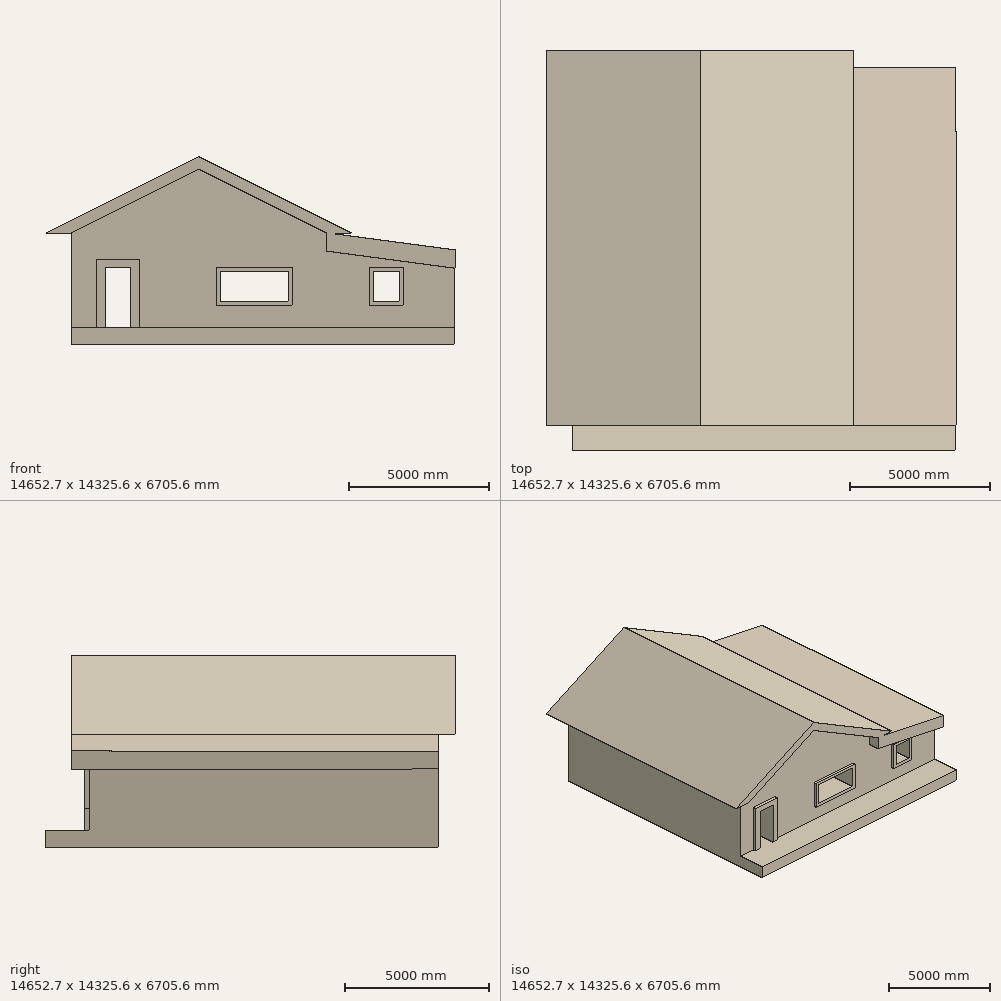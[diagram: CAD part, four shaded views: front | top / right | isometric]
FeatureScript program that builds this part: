
annotation { "Feature Type Name" : "Feature", "Feature Type Description" : "" }
export const myFeature = defineFeature(function(context is Context, id is Id, definition is map)
    precondition{}
    {
        {
            var Q0;
            Q0=qCreatedBy(makeId("Front.planeOp"),FACE);
            var sketch = newSketch(context, id + "F0", { "sketchPlane" : qUnion([Q0])});
            skLineSegment(sketch, "E0", {"start": v(0, 0) * mm, "end": v(4572, 0) * mm});
            skLineSegment(sketch, "E1", {"start": v(0, 0) * mm, "end": v(-4572, 0) * mm});
            skLineSegment(sketch, "E2", {"start": v(0, 0) * mm, "end": v(0, 2286) * mm});
            skLineSegment(sketch, "E3", {"start": v(0, 2286) * mm, "end": v(0, 2743.2) * mm});
            skLineSegment(sketch, "E4", {"start": v(-4572, 0) * mm, "end": v(-5486.4, 0) * mm});
            skLineSegment(sketch, "E5", {"start": v(4572, 0) * mm, "end": v(5486.4, 0) * mm});
            skLineSegment(sketch, "E6", {"start": v(0, 2286) * mm, "end": v(4572, 0) * mm});
            skLineSegment(sketch, "E7", {"start": v(0, 2286) * mm, "end": v(-4572, 0) * mm});
            skLineSegment(sketch, "E8", {"start": v(0, 2743.2) * mm, "end": v(-5486.4, 0) * mm});
            skLineSegment(sketch, "E9", {"start": v(0, 2743.2) * mm, "end": v(5486.4, 0) * mm});
            skLineSegment(sketch, "E10", {"start": v(-4572, 0) * mm, "end": v(-4572, -3352.8) * mm});
            skLineSegment(sketch, "E11", {"start": v(-4572, -3352.8) * mm, "end": v(4572, -3352.8) * mm});
            skLineSegment(sketch, "E12", {"start": v(4572, 0) * mm, "end": v(4572, -609.6) * mm});
            skLineSegment(sketch, "E13", {"start": v(4572, -609.6) * mm, "end": v(4572, -3352.8) * mm});
            skLineSegment(sketch, "E14", {"start": v(-4572, -3352.8) * mm, "end": v(-4572, -3962.4) * mm});
            skLineSegment(sketch, "E15", {"start": v(-4572, -3962.4) * mm, "end": v(4572, -3962.4) * mm});
            skLineSegment(sketch, "E16", {"start": v(4572, -3352.8) * mm, "end": v(4572, -3962.4) * mm});
            skLineSegment(sketch, "E17", {"start": v(4572, -3962.4) * mm, "end": v(9144, -3962.4) * mm});
            skLineSegment(sketch, "E18", {"start": v(4572, -3352.8) * mm, "end": v(9144, -3352.8) * mm});
            skLineSegment(sketch, "E19", {"start": v(9144, -3352.8) * mm, "end": v(9144, -3962.4) * mm});
            skLineSegment(sketch, "E20", {"start": v(9144, -3352.8) * mm, "end": v(9144, -609.6) * mm});
            skLineSegment(sketch, "E21", {"start": v(4572, 0) * mm, "end": v(9144, -609.6) * mm});
            skLineSegment(sketch, "E22", {"start": v(9144, -609.6) * mm, "end": v(9144, -1219.2) * mm});
            skLineSegment(sketch, "E23", {"start": v(4572, -609.6) * mm, "end": v(9144, -1219.2) * mm});
            skLineSegment(sketch, "E24", {"start": v(-3352.8, -3352.8) * mm, "end": v(-3352.8, -1219.2) * mm});
            skLineSegment(sketch, "E25", {"start": v(-2438.4, -3352.8) * mm, "end": v(-2438.4, -1219.2) * mm});
            skLineSegment(sketch, "E26", {"start": v(-2438.4, -1219.2) * mm, "end": v(-3352.8, -1219.2) * mm});
            skLineSegment(sketch, "E27", {"start": v(-3657.6, -3352.8) * mm, "end": v(-3657.6, -914.4) * mm});
            skLineSegment(sketch, "E28", {"start": v(-3657.6, -914.4) * mm, "end": v(-2133.6, -914.4) * mm});
            skLineSegment(sketch, "E29", {"start": v(-2133.6, -914.4) * mm, "end": v(-2133.6, -3352.8) * mm});
            skLineSegment(sketch, "E30.bottom", {"start": v(609.6, -1219.2) * mm, "end": v(3352.8, -1219.2) * mm});
            skLineSegment(sketch, "E30.top", {"start": v(609.6, -2590.8) * mm, "end": v(3352.8, -2590.8) * mm});
            skLineSegment(sketch, "E30.left", {"start": v(609.6, -1219.2) * mm, "end": v(609.6, -2590.8) * mm});
            skLineSegment(sketch, "E30.right", {"start": v(3352.8, -1219.2) * mm, "end": v(3352.8, -2590.8) * mm});
            skLineSegment(sketch, "E31.bottom", {"start": v(762, -1371.6) * mm, "end": v(3200.4, -1371.6) * mm});
            skLineSegment(sketch, "E31.top", {"start": v(762, -2438.4) * mm, "end": v(3200.4, -2438.4) * mm});
            skLineSegment(sketch, "E31.left", {"start": v(762, -1371.6) * mm, "end": v(762, -2438.4) * mm});
            skLineSegment(sketch, "E31.right", {"start": v(3200.4, -1371.6) * mm, "end": v(3200.4, -2438.4) * mm});
            skLineSegment(sketch, "E32.bottom", {"start": v(6096, -1219.2) * mm, "end": v(7315.2, -1219.2) * mm});
            skLineSegment(sketch, "E32.top", {"start": v(6096, -2590.8) * mm, "end": v(7315.2, -2590.8) * mm});
            skLineSegment(sketch, "E32.left", {"start": v(6096, -1219.2) * mm, "end": v(6096, -2590.8) * mm});
            skLineSegment(sketch, "E32.right", {"start": v(7315.2, -1219.2) * mm, "end": v(7315.2, -2590.8) * mm});
            skLineSegment(sketch, "E33.bottom", {"start": v(6248.4, -1371.6) * mm, "end": v(7162.8, -1371.6) * mm});
            skLineSegment(sketch, "E33.top", {"start": v(6248.4, -2438.4) * mm, "end": v(7162.8, -2438.4) * mm});
            skLineSegment(sketch, "E33.left", {"start": v(6248.4, -1371.6) * mm, "end": v(6248.4, -2438.4) * mm});
            skLineSegment(sketch, "E33.right", {"start": v(7162.8, -1371.6) * mm, "end": v(7162.8, -2438.4) * mm});
            skLineSegment(sketch, "E34", {"start": v(1746.97, 1869.71) * mm, "end": v(1746.97, 3393.71) * mm});
            skLineSegment(sketch, "E35", {"start": v(1746.97, 3393.71) * mm, "end": v(1137.37, 3393.71) * mm});
            skLineSegment(sketch, "E36", {"start": v(1137.37, 3393.71) * mm, "end": v(1137.37, 2174.51) * mm});
            skText(sketch, "E37", { "text": "Charles", "fontName": "AllertaStencil-Regular.ttf"});
            skLineSegment(sketch, "E38", {"start": v(-5486.4, 0) * mm, "end": v(-5486.4, 6096) * mm, "construction": true});
            const initialGuessF0  = {"E37": [-2.7432, 3.9624, 1, 0, 1.35413]};
            skSetInitialGuess(sketch, initialGuessF0);
            skSolve(sketch);
        }
        {
            var Q0;
            Q0=makeQuery(id+"F0.imprint","IMPRINT",FACE,{"disambiguationData":[TD([[makeQuery(id+"F0.imprint","IMPRINT",EDGE,{"derivedFrom":sQuery(id+"F0.wireOp",EDGE,"E1")}),-1.0]])]});
            var Q1;
            Q1=makeQuery(id+"F0.imprint","IMPRINT",FACE,{"disambiguationData":[TD([[makeQuery(id+"F0.imprint","IMPRINT",EDGE,{"derivedFrom":sQuery(id+"F0.wireOp",EDGE,"E0")}),1.0]])]});
            var Q2;
            Q2=makeQuery(id+"F0.imprint","IMPRINT",FACE,{"disambiguationData":[TD([[makeQuery(id+"F0.imprint","IMPRINT",EDGE,{"derivedFrom":sQuery(id+"F0.wireOp",EDGE,"E0")}),-1.0]])]});
            var Q3;
            Q3=makeQuery(id+"F0.imprint","IMPRINT",FACE,{"disambiguationData":[TD([[makeQuery(id+"F0.imprint","IMPRINT",EDGE,{"derivedFrom":sQuery(id+"F0.wireOp",EDGE,"E13")}),1.0]])]});
            extrude(context, id + "F1", {"entities" : qUnion([Q0, Q1, Q2, Q3]), "depth" : 12192 * mm, "offsetDistance" : 30.48 * mm});
        }
        {
            var Q0;
            {var subQ0=sQuery(id+"F0.wireOp",EDGE,"E24");Q0=makeQuery(id+"F0.imprint","IMPRINT",FACE,{"disambiguationData":[TD([[makeQuery(id+"F0.imprint","IMPRINT",EDGE,{"derivedFrom":subQ0}),1.0]])]});}
            var Q1;
            Q1=makeQuery(id+"F0.imprint","IMPRINT",FACE,{"disambiguationData":[TD([[makeQuery(id+"F0.imprint","IMPRINT",EDGE,{"derivedFrom":sQuery(id+"F0.wireOp",EDGE,"E30.bottom")}),-1.0]])]});
            var Q2;
            Q2=makeQuery(id+"F0.imprint","IMPRINT",FACE,{"disambiguationData":[TD([[makeQuery(id+"F0.imprint","IMPRINT",EDGE,{"derivedFrom":sQuery(id+"F0.wireOp",EDGE,"E32.bottom")}),-1.0]])]});
            extrude(context, id + "F2", {"entities" : qUnion([Q0, Q1, Q2]), "operationType" : NewBodyOperationType.ADD, "depth" : 12344.4 * mm, "offsetDistance" : 30.48 * mm});
        }
        {
            var Q0;
            Q0=makeQuery(id+"F0.imprint","IMPRINT",FACE,{"disambiguationData":[TD([[makeQuery(id+"F0.imprint","IMPRINT",EDGE,{"derivedFrom":sQuery(id+"F0.wireOp",EDGE,"E3")}),1.0]])]});
            var Q1;
            {var subQ1=sQuery(id+"F0.wireOp",EDGE,"E3");Q1=makeQuery(id+"F0.imprint","IMPRINT",FACE,{"disambiguationData":[TD([[makeQuery(id+"F0.imprint","IMPRINT",EDGE,{"derivedFrom":subQ1}),-1.0]])]});}
            extrude(context, id + "F3", {"entities" : qUnion([Q0, Q1]), "operationType" : NewBodyOperationType.ADD, "depth" : 12801.6 * mm, "offsetDistance" : 30.48 * mm, "hasSecondDirection" : true, "secondDirectionOppositeDirection" : true, "secondDirectionDepth" : 609.6 * mm});
        }
        {
            var Q0;
            {var subQ5=sQuery(id+"F0.wireOp",EDGE,"E14");Q0=makeQuery(id+"F0.imprint","IMPRINT",FACE,{"disambiguationData":[TD([[makeQuery(id+"F0.imprint","IMPRINT",EDGE,{"derivedFrom":subQ5}),1.0]])]});}
            var Q1;
            Q1=makeQuery(id+"F0.imprint","IMPRINT",FACE,{"disambiguationData":[TD([[makeQuery(id+"F0.imprint","IMPRINT",EDGE,{"derivedFrom":sQuery(id+"F0.wireOp",EDGE,"E16")}),1.0]])]});
            extrude(context, id + "F4", {"entities" : qUnion([Q0, Q1]), "operationType" : NewBodyOperationType.ADD, "depth" : 13716 * mm, "offsetDistance" : 30.48 * mm});
        }
        {
            var Q0;
            Q0=makeQuery(id+"F0.imprint","IMPRINT",FACE,{"disambiguationData":[TD([[makeQuery(id+"F0.imprint","IMPRINT",EDGE,{"derivedFrom":sQuery(id+"F0.wireOp",EDGE,"E12")}),1.0]])]});
            extrude(context, id + "F5", {"entities" : qUnion([Q0]), "operationType" : NewBodyOperationType.ADD, "depth" : 12801.6 * mm, "offsetDistance" : 30.48 * mm, "hasDraft" : true, "draftAngle" : .1 * degree});
        }
    });
